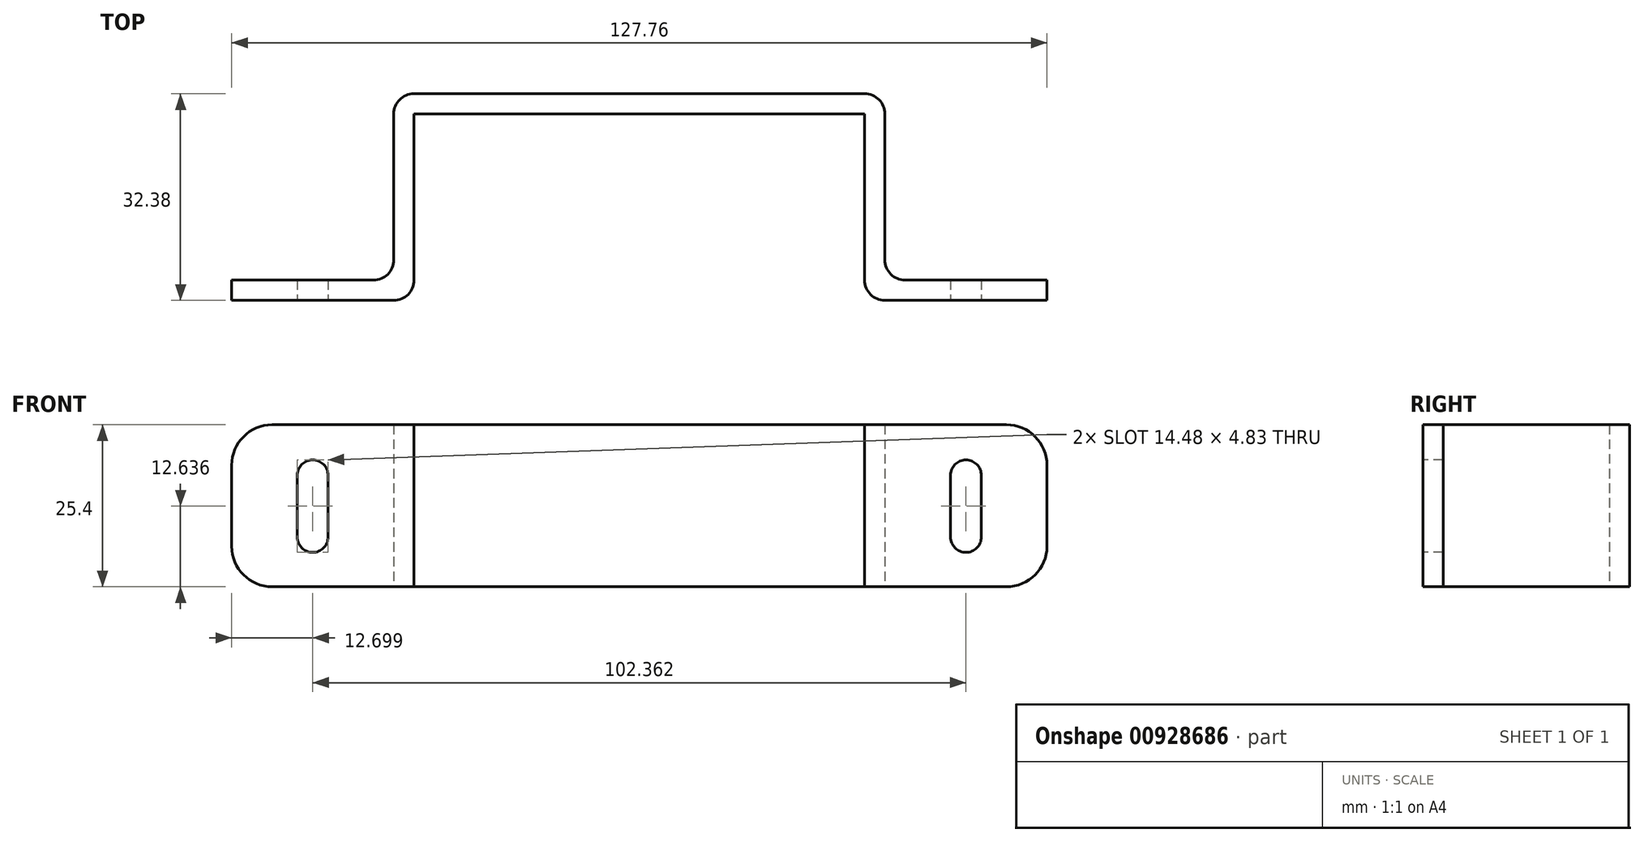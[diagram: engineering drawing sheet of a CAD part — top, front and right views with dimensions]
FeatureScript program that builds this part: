
annotation { "Feature Type Name" : "Feature", "Feature Type Description" : "" }
export const myFeature = defineFeature(function(context is Context, id is Id, definition is map)
    precondition{}
    {
        {
            var Q0;
            Q0=qCreatedBy(makeId("Top.planeOp"),FACE);
            var sketch = newSketch(context, id + "F0", { "sketchPlane" : qUnion([Q0])});
            skLineSegment(sketch, "E0", {"start": v(0, 29.21) * mm, "end": v(35.3, 29.21) * mm});
            skLineSegment(sketch, "E1", {"start": v(35.3, 29.21) * mm, "end": v(35.3, 0) * mm});
            skLineSegment(sketch, "E2", {"start": v(35.3, 0) * mm, "end": v(63.88, 0) * mm});
            skLineSegment(sketch, "E3.0", {"start": v(38.48, 3.17) * mm, "end": v(63.88, 3.17) * mm});
            skLineSegment(sketch, "E3.1", {"start": v(38.48, 32.39) * mm, "end": v(38.48, 3.18) * mm});
            skLineSegment(sketch, "E3.2", {"start": v(0, 32.39) * mm, "end": v(38.48, 32.39) * mm});
            skLineSegment(sketch, "E4", {"start": v(63.88, 3.18) * mm, "end": v(63.88, 0) * mm});
            skLineSegment(sketch, "E5.MirrorCS", {"start": v(-63.88, 3.18) * mm, "end": v(-63.88, 0) * mm});
            skLineSegment(sketch, "E6.MirrorCS", {"start": v(-35.3, 29.21) * mm, "end": v(-35.3, 0) * mm});
            skLineSegment(sketch, "E7.MirrorCS", {"start": v(0, 32.39) * mm, "end": v(-38.48, 32.39) * mm});
            skLineSegment(sketch, "E8.MirrorCS", {"start": v(-38.48, 3.17) * mm, "end": v(-63.88, 3.17) * mm});
            skLineSegment(sketch, "E9.MirrorCS", {"start": v(-35.3, 0) * mm, "end": v(-63.88, 0) * mm});
            skLineSegment(sketch, "E10.MirrorCS", {"start": v(0, 29.21) * mm, "end": v(-35.3, 29.21) * mm});
            skLineSegment(sketch, "E11.MirrorCS", {"start": v(-38.48, 32.39) * mm, "end": v(-38.48, 3.18) * mm});
            skSolve(sketch);
        }
        {
            var Q0;
            Q0=qSketchRegion(id+"F0",true);
            extrude(context, id + "F1", {"entities" : qUnion([Q0]), "depth" : 25.4 * mm, "offsetDistance" : 25.4 * mm});
        }
        {
            var Q0;
            Q0=makeQuery(id+"F1.opExtrude","SWEPT_EDGE",EDGE,{"disambiguationData":[OSD([sQuery(id+"F0.wireOp",EDGE,"E6.MirrorCS"),sQuery(id+"F0.wireOp",EDGE,"E9.MirrorCS")])]});
            var Q1;
            Q1=makeQuery(id+"F1.opExtrude","SWEPT_EDGE",EDGE,{"disambiguationData":[OSD([sQuery(id+"F0.wireOp",EDGE,"E1"),sQuery(id+"F0.wireOp",EDGE,"E2")])]});
            var Q2;
            Q2=makeQuery(id+"F1.opExtrude","SWEPT_EDGE",EDGE,{"disambiguationData":[OSD([sQuery(id+"F0.wireOp",EDGE,"E8.MirrorCS"),sQuery(id+"F0.wireOp",EDGE,"E11.MirrorCS")])]});
            var Q3;
            Q3=makeQuery(id+"F1.opExtrude","SWEPT_EDGE",EDGE,{"disambiguationData":[OSD([sQuery(id+"F0.wireOp",EDGE,"E7.MirrorCS"),sQuery(id+"F0.wireOp",EDGE,"E11.MirrorCS")])]});
            var Q4;
            Q4=makeQuery(id+"F1.opExtrude","SWEPT_EDGE",EDGE,{"disambiguationData":[OSD([sQuery(id+"F0.wireOp",EDGE,"E3.1"),sQuery(id+"F0.wireOp",EDGE,"E3.2")])]});
            var Q5;
            Q5=makeQuery(id+"F1.opExtrude","SWEPT_EDGE",EDGE,{"disambiguationData":[OSD([sQuery(id+"F0.wireOp",EDGE,"E3.0"),sQuery(id+"F0.wireOp",EDGE,"E3.1")])]});
            fillet(context, id + "F2", {"entities" : qUnion([Q0, Q1, Q2, Q3, Q4, Q5]), "radius" : 3.17 * mm, "tangentPropagation" : true, "allowEdgeOverflow" : false});
        }
        {
            var Q0;
            Q0=qCreatedBy(makeId("Front.planeOp"),FACE);
            var sketch = newSketch(context, id + "F3", { "sketchPlane" : qUnion([Q0])});
            skLineSegment(sketch, "E12", {"start": v(-51.18, 7.81) * mm, "end": v(-51.18, 17.46) * mm});
            skArc(sketch, "E13.0.startCap", {"start": v(-48.77, 7.81) * mm, "mid": v(-51.18, 5.4) * mm, "end": v(-53.6, 7.81) * mm});
            skArc(sketch, "E13.0.endCap", {"start": v(-53.6, 17.46) * mm, "mid": v(-51.18, 19.88) * mm, "end": v(-48.77, 17.46) * mm});
            skLineSegment(sketch, "E13.0.left", {"start": v(-53.6, 7.81) * mm, "end": v(-53.6, 17.46) * mm});
            skLineSegment(sketch, "E13.0.right", {"start": v(-48.77, 7.81) * mm, "end": v(-48.77, 17.46) * mm});
            skLineSegment(sketch, "E14.MirrorCS", {"start": v(48.77, 7.81) * mm, "end": v(48.77, 17.46) * mm});
            skLineSegment(sketch, "E15.MirrorCS", {"start": v(51.18, 7.81) * mm, "end": v(51.18, 17.46) * mm});
            skLineSegment(sketch, "E16.MirrorCS", {"start": v(53.6, 7.81) * mm, "end": v(53.6, 17.46) * mm});
            skArc(sketch, "E17.MirrorCS", {"start": v(53.6, 17.46) * mm, "mid": v(51.18, 19.88) * mm, "end": v(48.77, 17.46) * mm});
            skArc(sketch, "E18.MirrorCS", {"start": v(48.77, 7.81) * mm, "mid": v(51.18, 5.4) * mm, "end": v(53.6, 7.81) * mm});
            skSolve(sketch);
        }
        {
            var Q0;
            Q0=qSketchRegion(id+"F3",true);
            extrude(context, id + "F4", {"entities" : qUnion([Q0]), "operationType" : NewBodyOperationType.REMOVE, "endBound" : BoundingType.THROUGH_ALL, "oppositeDirection" : true, "depth" : 25.4 * mm, "offsetDistance" : 25.4 * mm});
        }
        {
            var Q0;
            Q0=makeQuery(id+"F1.opExtrude","CAP_EDGE",EDGE,{"disambiguationData":[OSD([sQuery(id+"F0.wireOp",EDGE,"E5.MirrorCS")])],"isStart":true});
            var Q1;
            Q1=makeQuery(id+"F1.opExtrude","CAP_EDGE",EDGE,{"disambiguationData":[OSD([sQuery(id+"F0.wireOp",EDGE,"E5.MirrorCS")])],"isStart":false});
            var Q2;
            Q2=makeQuery(id+"F1.opExtrude","CAP_EDGE",EDGE,{"disambiguationData":[OSD([sQuery(id+"F0.wireOp",EDGE,"E4")])],"isStart":false});
            var Q3;
            Q3=makeQuery(id+"F1.opExtrude","CAP_EDGE",EDGE,{"disambiguationData":[OSD([sQuery(id+"F0.wireOp",EDGE,"E4")])],"isStart":true});
            fillet(context, id + "F5", {"entities" : qUnion([Q0, Q1, Q2, Q3]), "radius" : 6.35 * mm, "tangentPropagation" : true, "allowEdgeOverflow" : false});
        }
    });
